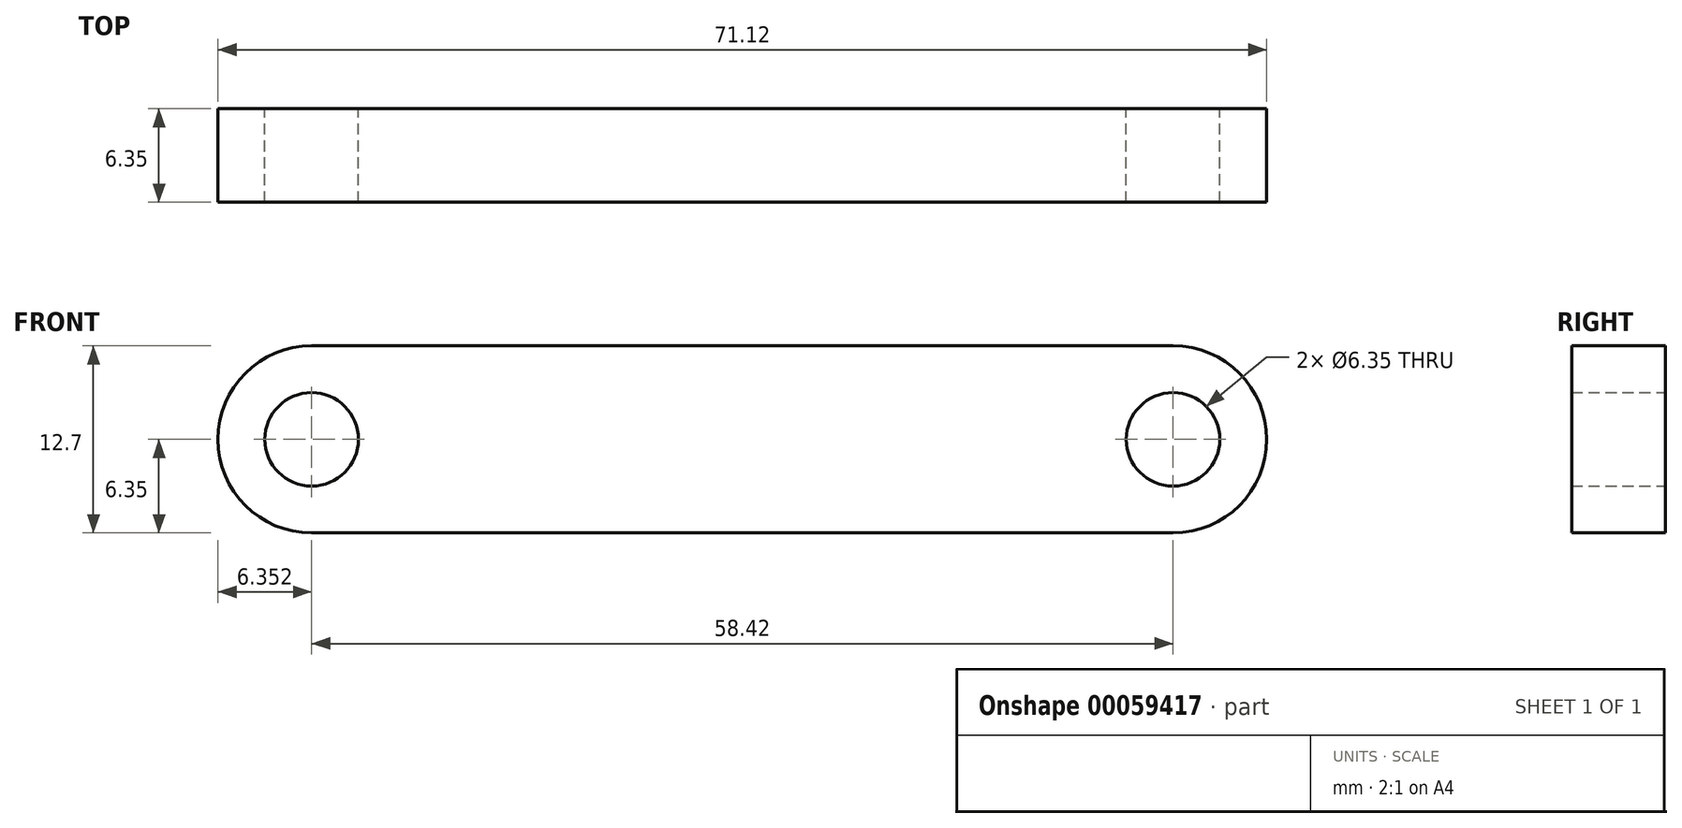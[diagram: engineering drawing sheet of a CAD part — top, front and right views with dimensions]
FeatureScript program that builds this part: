
annotation { "Feature Type Name" : "Feature", "Feature Type Description" : "" }
export const myFeature = defineFeature(function(context is Context, id is Id, definition is map)
    precondition{}
    {
        {
            var Q0;
            Q0=qCreatedBy(makeId("Front.planeOp"),FACE);
            var sketch = newSketch(context, id + "F0", { "sketchPlane" : qUnion([Q0])});
            skLineSegment(sketch, "E0", {"start": v(-20.4, 0) * mm, "end": v(26.84, 0) * mm, "construction": true});
            skCircle(sketch, "E1", {"center": v(-13.4, 0) * mm, "radius": 3.18 * mm});
            skCircle(sketch, "E2", {"center": v(45.02, 0) * mm, "radius": 3.18 * mm});
            skArc(sketch, "E3", {"start": v(-13.4, 6.35) * mm, "mid": v(-19.75, 0) * mm, "end": v(-13.4, -6.35) * mm});
            skArc(sketch, "E4", {"start": v(45.02, -6.35) * mm, "mid": v(51.37, 0) * mm, "end": v(45.02, 6.35) * mm});
            skLineSegment(sketch, "E5", {"start": v(-13.4, 6.35) * mm, "end": v(45.02, 6.35) * mm});
            skLineSegment(sketch, "E6", {"start": v(-13.4, -6.35) * mm, "end": v(45.02, -6.35) * mm});
            skSolve(sketch);
        }
        {
            var Q0;
            Q0 = qSketchRegion(id + "F0", true);
            extrude(context, id + "F1", {"entities" : qUnion([Q0]), "depth" : 6.35 * mm});
        }
    });
